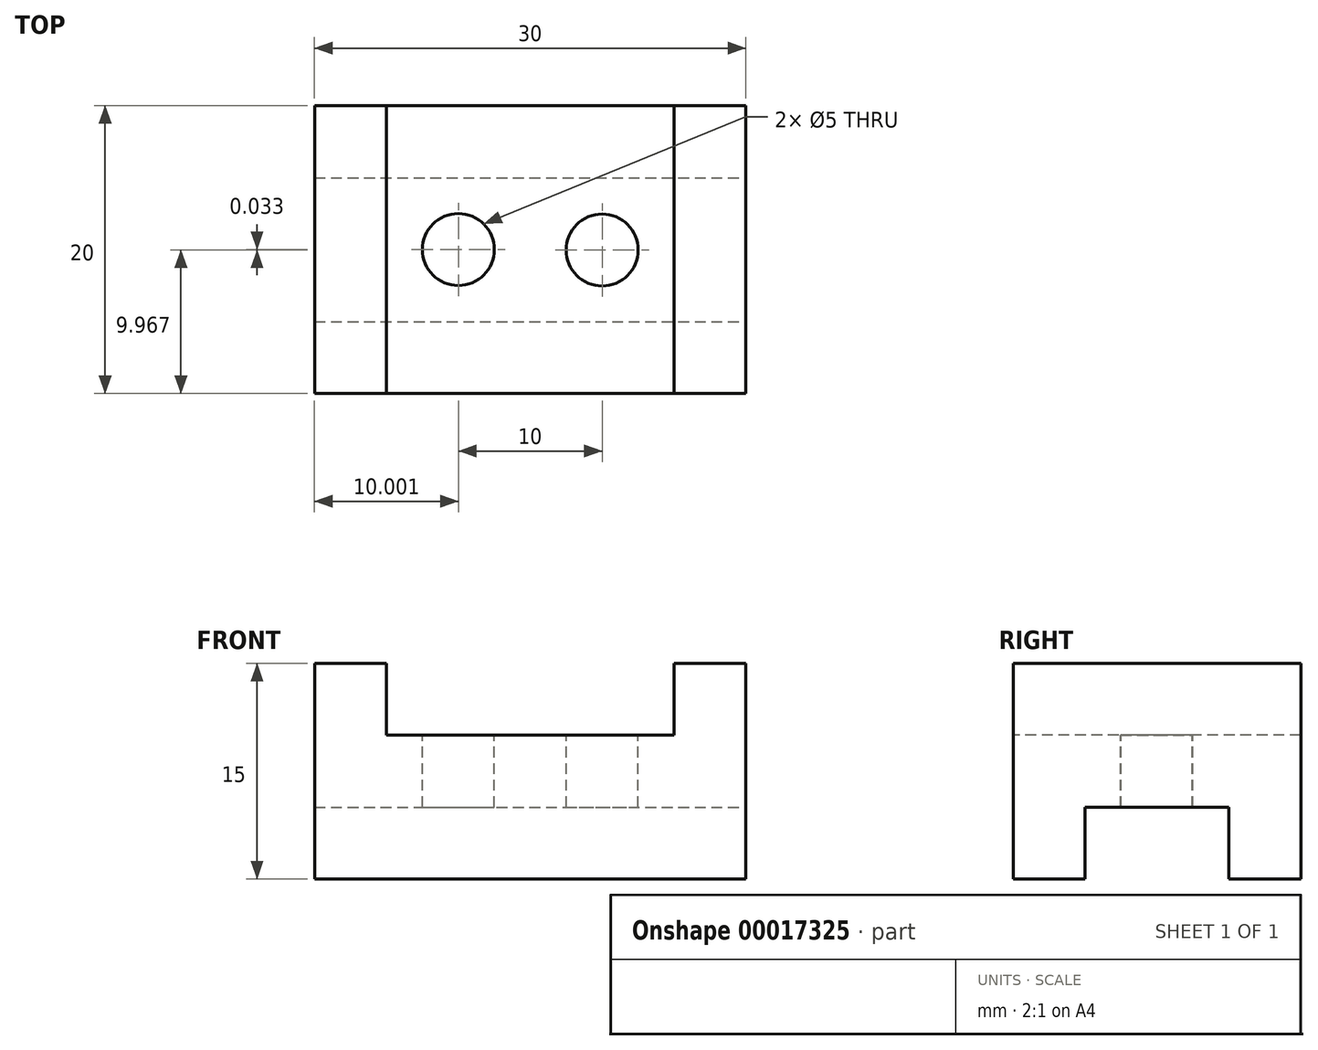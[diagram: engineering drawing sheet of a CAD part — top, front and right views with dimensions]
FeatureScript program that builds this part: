
annotation { "Feature Type Name" : "Feature", "Feature Type Description" : "" }
export const myFeature = defineFeature(function(context is Context, id is Id, definition is map)
    precondition{}
    {
        {
            var Q0;
            Q0=qCreatedBy(makeId("Front.planeOp"),FACE);
            var sketch = newSketch(context, id + "F0", { "sketchPlane" : qUnion([Q0])});
            skLineSegment(sketch, "E0", {"start": v(-18.15, -10.76) * mm, "end": v(11.85, -10.76) * mm});
            skLineSegment(sketch, "E1", {"start": v(11.85, -10.76) * mm, "end": v(11.85, 4.24) * mm});
            skLineSegment(sketch, "E2", {"start": v(11.85, 4.24) * mm, "end": v(6.85, 4.24) * mm});
            skLineSegment(sketch, "E3", {"start": v(6.85, 4.24) * mm, "end": v(6.85, -0.76) * mm});
            skLineSegment(sketch, "E4", {"start": v(6.85, -0.76) * mm, "end": v(-13.15, -0.76) * mm});
            skLineSegment(sketch, "E5", {"start": v(-13.15, -0.76) * mm, "end": v(-13.15, 4.24) * mm});
            skLineSegment(sketch, "E6", {"start": v(-13.15, 4.24) * mm, "end": v(-18.15, 4.24) * mm});
            skLineSegment(sketch, "E7", {"start": v(-18.15, 4.24) * mm, "end": v(-18.15, -10.76) * mm});
            skSolve(sketch);
        }
        {
            var Q0;
            Q0=makeQuery(id+"F0.imprint","IMPRINT",FACE,{"disambiguationData":[TD([[makeQuery(id+"F0.imprint","IMPRINT",EDGE,{"derivedFrom":sQuery(id+"F0.wireOp",EDGE,"E0")}),1.0]])]});
            extrude(context, id + "F1", {"entities" : qUnion([Q0]), "oppositeDirection" : true, "depth" : 20 * mm});
        }
        {
            var Q0;
            Q0=makeQuery(id+"F1.opExtrude","SWEPT_FACE",FACE,{"disambiguationData":[OSD([sQuery(id+"F0.wireOp",EDGE,"E1")])]});
            var sketch = newSketch(context, id + "F2", { "sketchPlane" : qUnion([Q0])});
            skLineSegment(sketch, "E8", {"start": v(5, -10.76) * mm, "end": v(5, -5.76) * mm});
            skLineSegment(sketch, "E9", {"start": v(5, -5.76) * mm, "end": v(15, -5.76) * mm});
            skLineSegment(sketch, "E10", {"start": v(15, -5.76) * mm, "end": v(15, -10.76) * mm});
            skLineSegment(sketch, "E11", {"start": v(5, -10.76) * mm, "end": v(15, -10.76) * mm});
            skSolve(sketch);
        }
        {
            var Q0;
            Q0=makeQuery(id+"F2.imprint","IMPRINT",FACE,{"disambiguationData":[TD([[makeQuery(id+"F2.imprint","IMPRINT",EDGE,{"derivedFrom":sQuery(id+"F2.wireOp",EDGE,"E8")}),-1.0]])]});
            extrude(context, id + "F3", {"entities" : qUnion([Q0]), "operationType" : NewBodyOperationType.REMOVE, "oppositeDirection" : true, "depth" : 30 * mm});
        }
        {
            var Q0;
            Q0=makeQuery(id+"F1.opExtrude","SWEPT_FACE",FACE,{"disambiguationData":[OSD([sQuery(id+"F0.wireOp",EDGE,"E4")])]});
            var sketch = newSketch(context, id + "F4", { "sketchPlane" : qUnion([Q0])});
            skPoint(sketch, "E12", {"position": v(-8.15, 10) * mm});
            skPoint(sketch, "E13", {"position": v(1.85, 9.97) * mm});
            skSolve(sketch);
        }
        {
            var Q0;
            Q0=sQuery(id+"F4.wireOp",VERTEX,"E12");
            var Q1;
            Q1=sQuery(id+"F4.wireOp",VERTEX,"E13");
            var Q2;
            Q2=makeQuery(id+"F1.opExtrude","SWEPT_BODY",BODY,{"disambiguationData":[OSD([sQuery(id+"F0.wireOp",EDGE,"E0"),sQuery(id+"F0.wireOp",EDGE,"E1"),sQuery(id+"F0.wireOp",EDGE,"E2"),sQuery(id+"F0.wireOp",EDGE,"E3"),sQuery(id+"F0.wireOp",EDGE,"E4"),sQuery(id+"F0.wireOp",EDGE,"E5"),sQuery(id+"F0.wireOp",EDGE,"E6"),sQuery(id+"F0.wireOp",EDGE,"E7")])]});
            hole(context, id + "F5", {"style" : HoleStyle.SIMPLE, "holeDiameter" : 5 * mm, "endStyle" : HoleEndStyle.THROUGH, "locations" : qUnion([Q0, Q1]), "scope" : qUnion([Q2])});
        }
    });
